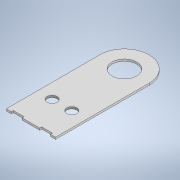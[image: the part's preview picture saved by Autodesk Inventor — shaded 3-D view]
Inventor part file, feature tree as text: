
AUTODESK INVENTOR PART (.ipt)
format: ipt  version: 2022 (Build 260153000, 153)  size: 139,776 bytes
history: native  units: mm
features: sheet_metal_op x1, sketch x1, other x1
ambient origin geometry x8: Origin, YZ Plane, XZ Plane, XY Plane, X Axis, Y Axis, Z Axis, Center Point
bodies: Body1 (feature_tree)
feature tree (3):
  sheet_metal_op  "Face2"
  sketch  "Sketch1"  dims[d0=10.2mm d1=25.0mm d2=2.0mm d3=2.0mm d6=5.0mm d7=11.0mm d8=5.0mm d9=11.0mm d10=50.0mm d12=25.0mm d13=120.0mm d14=31.5mm d16=10.2mm d17=31.5mm d18=20.0mm d19=15.0mm d20=2.0mm]
  other  "Plate2"
